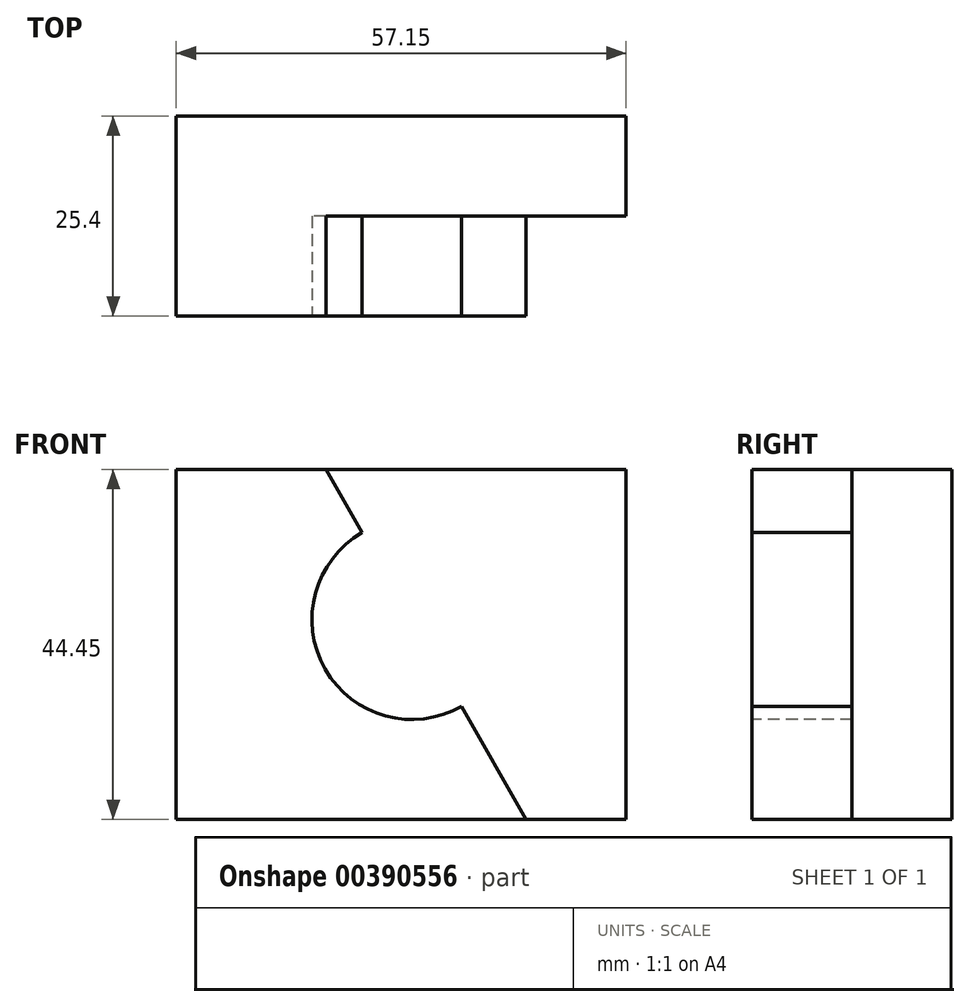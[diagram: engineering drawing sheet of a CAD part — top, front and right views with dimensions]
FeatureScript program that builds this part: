
annotation { "Feature Type Name" : "Feature", "Feature Type Description" : "" }
export const myFeature = defineFeature(function(context is Context, id is Id, definition is map)
    precondition{}
    {
        {
            var Q0;
            Q0=qCreatedBy(makeId("Front.planeOp"),FACE);
            var sketch = newSketch(context, id + "F0", { "sketchPlane" : qUnion([Q0])});
            skLineSegment(sketch, "E0", {"start": v(0, 0) * mm, "end": v(57.15, 0) * mm});
            skLineSegment(sketch, "E1", {"start": v(57.15, 0) * mm, "end": v(57.15, 44.45) * mm});
            skLineSegment(sketch, "E2", {"start": v(57.15, 44.45) * mm, "end": v(0, 44.45) * mm});
            skLineSegment(sketch, "E3", {"start": v(0, 44.45) * mm, "end": v(0, 0) * mm});
            skSolve(sketch);
        }
        {
            var Q0;
            Q0 = qSketchRegion(id + "F0", true);
            extrude(context, id + "F1", {"entities" : qUnion([Q0]), "depth" : 25.4 * mm});
        }
        {
            var Q0;
            Q0=makeQuery(id+"F1.opExtrude","CAP_FACE",FACE,{"disambiguationData":[OSD([sQuery(id+"F0.wireOp",EDGE,"E0"),sQuery(id+"F0.wireOp",EDGE,"E1"),sQuery(id+"F0.wireOp",EDGE,"E2"),sQuery(id+"F0.wireOp",EDGE,"E3")])],"isStart":false});
            var sketch = newSketch(context, id + "F2", { "sketchPlane" : qUnion([Q0])});
            skLineSegment(sketch, "E4", {"start": v(19.05, 44.45) * mm, "end": v(44.45, 0) * mm});
            skSolve(sketch);
        }
        {
            var Q0;
            Q0 = qSketchRegion(id + "F2", true);
            var Q1;
            {var subQ0=sQuery(id+"F2.wireOp",EDGE,"E4");Q1=makeQuery(id+"F2.imprint","IMPRINT",FACE,{"disambiguationData":[TD([[makeQuery(id+"F2.imprint","IMPRINT",EDGE,{"derivedFrom":subQ0}),1.0]])]});}
            extrude(context, id + "F3", {"entities" : qUnion([Q0, Q1]), "operationType" : NewBodyOperationType.REMOVE, "oppositeDirection" : true, "depth" : 12.7 * mm});
        }
        {
            var Q0;
            Q0=makeQuery(id+"F1.opExtrude","CAP_FACE",FACE,{"disambiguationData":[OSD([sQuery(id+"F0.wireOp",EDGE,"E0"),sQuery(id+"F0.wireOp",EDGE,"E1"),sQuery(id+"F0.wireOp",EDGE,"E2"),sQuery(id+"F0.wireOp",EDGE,"E3")])],"isStart":false});
            var sketch = newSketch(context, id + "F4", { "sketchPlane" : qUnion([Q0])});
            skCircle(sketch, "E5", {"center": v(29.94, 25.4) * mm, "radius": 12.7 * mm});
            skSolve(sketch);
        }
        {
            var Q0;
            {var subQ0=sQuery(id+"F4.wireOp",EDGE,"E5");var subQ1=makeQuery(id+"F3.boolean.opBoolean","COPY",EDGE,{"derivedFrom":makeQuery(id+"F3.opExtrude","CAP_EDGE",EDGE,{"disambiguationData":[OSD([sQuery(id+"F2.wireOp",EDGE,"E4")])],"isStart":true})});var subQ2=makeQuery(id+"F4.imprint","INTERSECT",VERTEX,{"disambiguationData":[OD(0.0)],"derivedFrom":[subQ1,subQ0]});Q0=makeQuery(id+"F4.imprint","IMPRINT",FACE,{"disambiguationData":[TD([[makeQuery(id+"F4.imprint","IMPRINT",EDGE,{"disambiguationData":[TD([[subQ2,-1.0]])],"derivedFrom":subQ0}),1.0]])]});}
            extrude(context, id + "F5", {"entities" : qUnion([Q0]), "operationType" : NewBodyOperationType.REMOVE, "oppositeDirection" : true, "depth" : 12.7 * mm});
        }
    });
